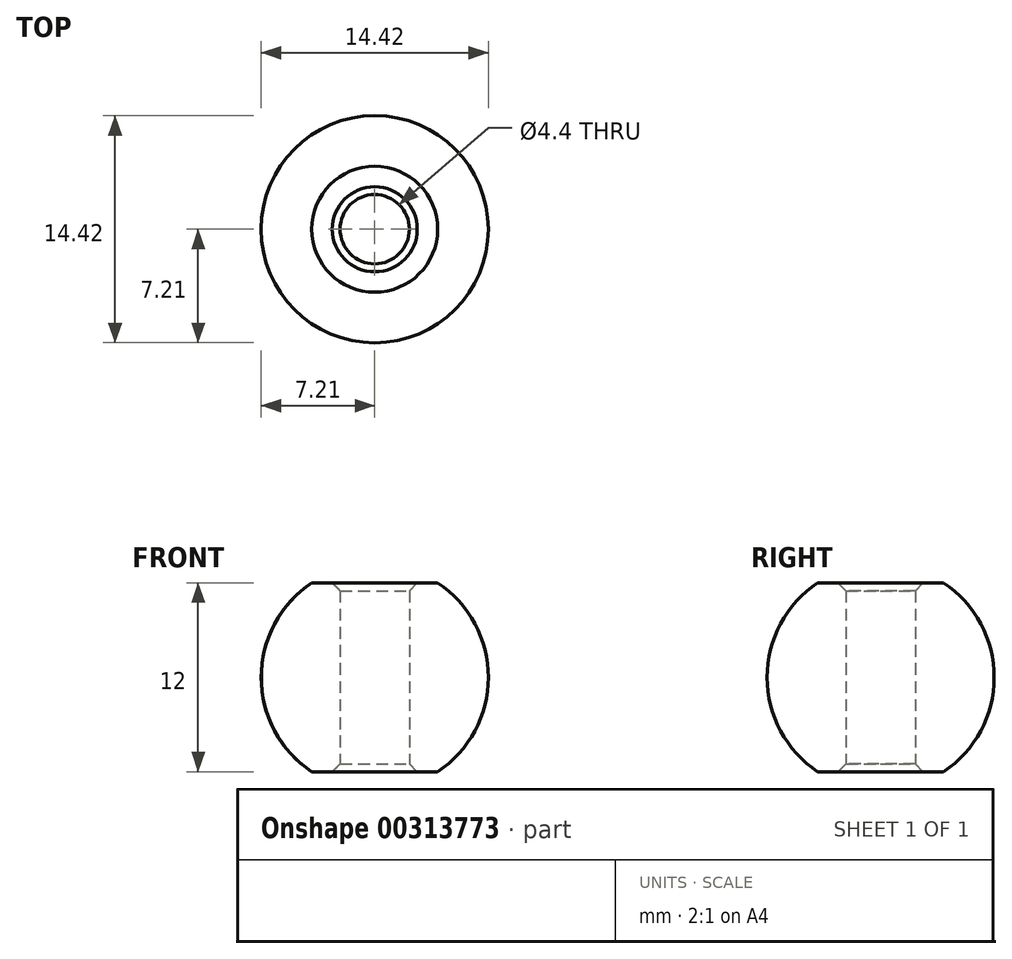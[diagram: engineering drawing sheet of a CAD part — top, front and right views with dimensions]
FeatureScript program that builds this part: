
annotation { "Feature Type Name" : "Feature", "Feature Type Description" : "" }
export const myFeature = defineFeature(function(context is Context, id is Id, definition is map)
    precondition{}
    {
        {
            var Q0;
            Q0=qCreatedBy(makeId("Front.planeOp"),FACE);
            var sketch = newSketch(context, id + "F0", { "sketchPlane" : qUnion([Q0])});
            skLineSegment(sketch, "E0", {"start": v(0, 0) * mm, "end": v(0, 12) * mm, "construction": true});
            skLineSegment(sketch, "E1", {"start": v(2.2, 0) * mm, "end": v(2.2, 12) * mm});
            skLineSegment(sketch, "E2", {"start": v(2.2, 12) * mm, "end": v(4, 12) * mm});
            skLineSegment(sketch, "E3", {"start": v(2.2, 0) * mm, "end": v(4, 0) * mm});
            skLineSegment(sketch, "E4", {"start": v(4, 12) * mm, "end": v(4, 0) * mm, "construction": true});
            skArc(sketch, "E5", {"start": v(4, 0) * mm, "mid": v(7.21, 6) * mm, "end": v(4, 12) * mm});
            skSolve(sketch);
        }
        {
            var Q0;
            Q0 = qSketchRegion(id + "F0", true);
            var Q1;
            Q1=sQuery(id+"F0.wireOp",EDGE,"E0");
            revolve(context, id + "F1", {"entities" : qUnion([Q0]), "axis" : qUnion([Q1]), "revolveType" : RevolveType.FULL});
        }
        {
            var Q0;
            Q0=makeQuery(id+"F1.opRevolve","SWEPT_EDGE",EDGE,{"disambiguationData":[OSD([sQuery(id+"F0.wireOp",EDGE,"E1"),sQuery(id+"F0.wireOp",EDGE,"E2")])]});
            var Q1;
            Q1=makeQuery(id+"F1.opRevolve","SWEPT_EDGE",EDGE,{"disambiguationData":[OSD([sQuery(id+"F0.wireOp",EDGE,"E1"),sQuery(id+"F0.wireOp",EDGE,"E3")])]});
            chamfer(context, id + "F2", {"entities" : qUnion([Q0, Q1]), "width" : 0.5 * mm, "tangentPropagation" : true});
        }
    });
